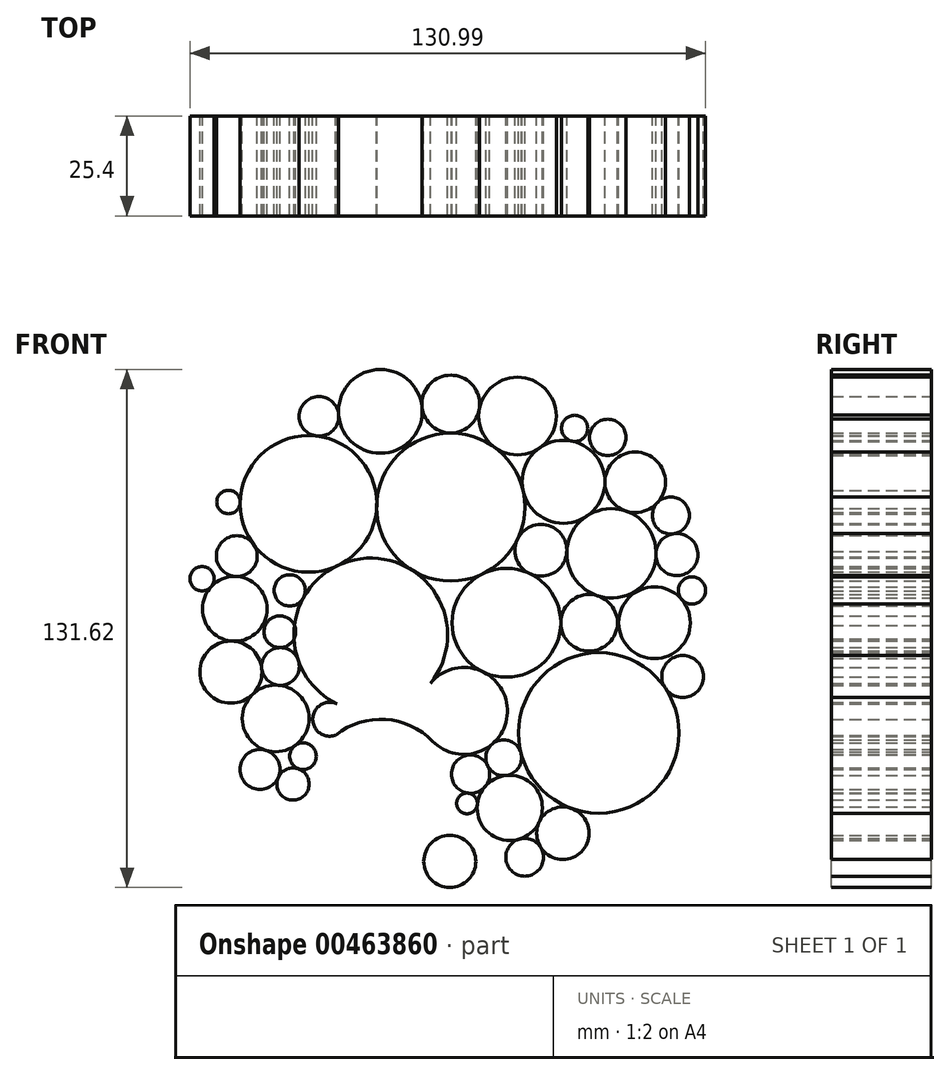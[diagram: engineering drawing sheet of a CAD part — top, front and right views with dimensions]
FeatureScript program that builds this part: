
annotation { "Feature Type Name" : "Feature", "Feature Type Description" : "" }
export const myFeature = defineFeature(function(context is Context, id is Id, definition is map)
    precondition{}
    {
        {
            var Q0;
            Q0=qCreatedBy(makeId("Front.planeOp"),FACE);
            var sketch = newSketch(context, id + "F0", { "sketchPlane" : qUnion([Q0])});
            skCircle(sketch, "E0", {"center": v(0, 0) * mm, "radius": 67.26 * mm});
            skCircle(sketch, "E1", {"center": v(-17.9, 53.72) * mm, "radius": 10.64 * mm});
            skCircle(sketch, "E2", {"center": v(-36.15, 30.22) * mm, "radius": 17.35 * mm});
            skCircle(sketch, "E3", {"center": v(46.85, 35.7) * mm, "radius": 7.69 * mm});
            skCircle(sketch, "E4", {"center": v(40.82, 17.65) * mm, "radius": 11.35 * mm});
            skCircle(sketch, "E5", {"center": v(0, 29.4) * mm, "radius": 18.81 * mm});
            skCircle(sketch, "E6", {"center": v(37.58, -28) * mm, "radius": 20.4 * mm});
            skCircle(sketch, "E7", {"center": v(-63.2, 11.2) * mm, "radius": 3.08 * mm});
            skArc(sketch, "E8", {"start": v(54.82, -38.89) * mm, "mid": v(54.84, -38.9) * mm, "end": v(54.86, -38.91) * mm});
            skCircle(sketch, "E9", {"center": v(-20.34, -3.08) * mm, "radius": 19.52 * mm});
            skCircle(sketch, "E10", {"center": v(14.13, 0) * mm, "radius": 13.81 * mm});
            skCircle(sketch, "E11", {"center": v(16.95, 52.54) * mm, "radius": 9.87 * mm});
            skCircle(sketch, "E12", {"center": v(-55.87, -12.54) * mm, "radius": 7.89 * mm});
            skCircle(sketch, "E13", {"center": v(51.75, 0) * mm, "radius": 9.1 * mm});
            skCircle(sketch, "E14", {"center": v(28.63, 35.82) * mm, "radius": 10.53 * mm});
            skCircle(sketch, "E15", {"center": v(28.48, -53.48) * mm, "radius": 6.67 * mm});
            skCircle(sketch, "E16", {"center": v(3.34, -22.4) * mm, "radius": 11.05 * mm});
            skCircle(sketch, "E17", {"center": v(13.44, -34.29) * mm, "radius": 4.55 * mm});
            skCircle(sketch, "E18", {"center": v(-44.5, -24.3) * mm, "radius": 8.48 * mm});
            skCircle(sketch, "E19", {"center": v(-54.9, 3.54) * mm, "radius": 8.21 * mm});
            skCircle(sketch, "E20", {"center": v(-33.5, 52.44) * mm, "radius": 5.03 * mm});
            skCircle(sketch, "E21", {"center": v(35.14, 0) * mm, "radius": 7.2 * mm});
            skCircle(sketch, "E22", {"center": v(-0.25, -60.64) * mm, "radius": 6.62 * mm});
            skCircle(sketch, "E23", {"center": v(57.44, 17.33) * mm, "radius": 5.35 * mm});
            skCircle(sketch, "E24", {"center": v(58.9, -13.65) * mm, "radius": 5.3 * mm});
            skCircle(sketch, "E25", {"center": v(22.9, 18.42) * mm, "radius": 6.59 * mm});
            skCircle(sketch, "E26", {"center": v(-54.36, 16.93) * mm, "radius": 5.2 * mm});
            skCircle(sketch, "E27", {"center": v(-56.48, 30.68) * mm, "radius": 2.98 * mm});
            skCircle(sketch, "E28", {"center": v(-43.42, -2.28) * mm, "radius": 4.03 * mm});
            skCircle(sketch, "E29", {"center": v(-43.28, -11.1) * mm, "radius": 4.79 * mm});
            skCircle(sketch, "E30", {"center": v(-48.49, -37.27) * mm, "radius": 5.08 * mm});
            skCircle(sketch, "E31", {"center": v(31.47, 49.4) * mm, "radius": 3.33 * mm});
            skCircle(sketch, "E32", {"center": v(0, 55.57) * mm, "radius": 7.35 * mm});
            skCircle(sketch, "E33", {"center": v(14.98, -47.04) * mm, "radius": 8.3 * mm});
            skCircle(sketch, "E34", {"center": v(-30.76, -24.52) * mm, "radius": 4.32 * mm});
            skCircle(sketch, "E35", {"center": v(-40.1, -40.97) * mm, "radius": 4.09 * mm});
            skCircle(sketch, "E36", {"center": v(18.77, -59.57) * mm, "radius": 4.8 * mm});
            skCircle(sketch, "E37", {"center": v(55.9, 27.26) * mm, "radius": 4.7 * mm});
            skCircle(sketch, "E38", {"center": v(61.26, 8.22) * mm, "radius": 3.46 * mm});
            skCircle(sketch, "E39", {"center": v(-17.75, -42.85) * mm, "radius": 18.33 * mm});
            skCircle(sketch, "E40", {"center": v(-40.92, 8.24) * mm, "radius": 3.97 * mm});
            skCircle(sketch, "E41", {"center": v(5.02, -38.46) * mm, "radius": 4.85 * mm});
            skCircle(sketch, "E42", {"center": v(4.1, -45.9) * mm, "radius": 2.64 * mm});
            skCircle(sketch, "E43", {"center": v(39.89, 47.1) * mm, "radius": 4.62 * mm});
            skCircle(sketch, "E44", {"center": v(-37.54, -33.9) * mm, "radius": 3.38 * mm});
            skSolve(sketch);
        }
        {
            var Q0;
            {var subQ0=sQuery(id+"F0.wireOp",EDGE,"E5");var subQ6=makeQuery(id+"F0.imprint","INTERSECT",VERTEX,{"derivedFrom":[subQ0,sQuery(id+"F0.wireOp",EDGE,"E11")]});Q0=makeQuery(id+"F0.imprint","IMPRINT",FACE,{"disambiguationData":[TD([[makeQuery(id+"F0.imprint","IMPRINT",EDGE,{"disambiguationData":[TD([[subQ6,1.0]])],"derivedFrom":subQ0}),1.0]])]});}
            var sketch = newSketch(context, id + "F1", { "sketchPlane" : qUnion([Q0])});
            skSolve(sketch);
        }
        {
            var Q0;
            Q0 = qSketchRegion(id + "F1", true);
            var Q1;
            {var subQ0=sQuery(id+"F0.wireOp",EDGE,"E5");var subQ4=makeQuery(id+"F0.imprint","INTERSECT",VERTEX,{"derivedFrom":[subQ0,sQuery(id+"F0.wireOp",EDGE,"E11")]});Q1=makeQuery(id+"F1.imprint","IMPRINT",FACE,{"disambiguationData":[TD([[makeQuery(id+"F1.imprint","IMPRINT",EDGE,{"derivedFrom":makeQuery(id+"F0.imprint","IMPRINT",EDGE,{"disambiguationData":[TD([[subQ4,1.0]])],"derivedFrom":subQ0})}),1.0]])]});}
            var Q2;
            {var subQ0=sQuery(id+"F0.wireOp",EDGE,"E2");var subQ4=makeQuery(id+"F0.imprint","INTERSECT",VERTEX,{"derivedFrom":[subQ0,sQuery(id+"F0.wireOp",EDGE,"E27")]});Q2=makeQuery(id+"F0.imprint","IMPRINT",FACE,{"disambiguationData":[TD([[makeQuery(id+"F0.imprint","IMPRINT",EDGE,{"disambiguationData":[TD([[subQ4,1.0]])],"derivedFrom":subQ0}),1.0]])]});}
            var Q3;
            {var subQ0=sQuery(id+"F0.wireOp",EDGE,"E1");var subQ1=makeQuery(id+"F0.imprint","INTERSECT",VERTEX,{"derivedFrom":[sQuery(id+"F0.wireOp",EDGE,"E0"),subQ0]});Q3=makeQuery(id+"F0.imprint","IMPRINT",FACE,{"disambiguationData":[TD([[makeQuery(id+"F0.imprint","IMPRINT",EDGE,{"disambiguationData":[TD([[subQ1,1.0]])],"derivedFrom":subQ0}),1.0]])]});}
            var Q4;
            {var subQ0=sQuery(id+"F0.wireOp",EDGE,"E32");var subQ1=makeQuery(id+"F0.imprint","INTERSECT",VERTEX,{"derivedFrom":[sQuery(id+"F0.wireOp",EDGE,"E1"),subQ0]});Q4=makeQuery(id+"F0.imprint","IMPRINT",FACE,{"disambiguationData":[TD([[makeQuery(id+"F0.imprint","IMPRINT",EDGE,{"disambiguationData":[TD([[subQ1,-1.0]])],"derivedFrom":subQ0}),1.0]])]});}
            var Q5;
            {var subQ0=sQuery(id+"F0.wireOp",EDGE,"E15");var subQ1=makeQuery(id+"F0.imprint","INTERSECT",VERTEX,{"derivedFrom":[sQuery(id+"F0.wireOp",EDGE,"E6"),subQ0]});Q5=makeQuery(id+"F0.imprint","IMPRINT",FACE,{"disambiguationData":[TD([[makeQuery(id+"F0.imprint","IMPRINT",EDGE,{"disambiguationData":[TD([[subQ1,-1.0]])],"derivedFrom":subQ0}),1.0]])]});}
            var Q6;
            {var subQ0=sQuery(id+"F0.wireOp",EDGE,"E6");var subQ5=makeQuery(id+"F0.imprint","INTERSECT",VERTEX,{"derivedFrom":[subQ0,sQuery(id+"F0.wireOp",EDGE,"E24")]});Q6=makeQuery(id+"F0.imprint","IMPRINT",FACE,{"disambiguationData":[TD([[makeQuery(id+"F0.imprint","IMPRINT",EDGE,{"disambiguationData":[TD([[subQ5,-1.0]])],"derivedFrom":subQ0}),1.0]])]});}
            var Q7;
            {var subQ0=sQuery(id+"F0.wireOp",EDGE,"E21");var subQ1=makeQuery(id+"F0.imprint","INTERSECT",VERTEX,{"derivedFrom":[sQuery(id+"F0.wireOp",EDGE,"E4"),subQ0]});Q7=makeQuery(id+"F0.imprint","IMPRINT",FACE,{"disambiguationData":[TD([[makeQuery(id+"F0.imprint","IMPRINT",EDGE,{"disambiguationData":[TD([[subQ1,-1.0]])],"derivedFrom":subQ0}),1.0]])]});}
            var Q8;
            {var subQ0=sQuery(id+"F0.wireOp",EDGE,"E4");var subQ4=makeQuery(id+"F0.imprint","INTERSECT",VERTEX,{"derivedFrom":[sQuery(id+"F0.wireOp",EDGE,"E3"),subQ0]});Q8=makeQuery(id+"F0.imprint","IMPRINT",FACE,{"disambiguationData":[TD([[makeQuery(id+"F0.imprint","IMPRINT",EDGE,{"disambiguationData":[TD([[subQ4,1.0]])],"derivedFrom":subQ0}),1.0]])]});}
            var Q9;
            Q9=makeQuery(id+"F0.imprint","IMPRINT",FACE,{"disambiguationData":[TD([[makeQuery(id+"F0.imprint","IMPRINT",EDGE,{"derivedFrom":sQuery(id+"F0.wireOp",EDGE,"E13")}),1.0]])]});
            var Q10;
            Q10=makeQuery(id+"F0.imprint","IMPRINT",FACE,{"disambiguationData":[TD([[makeQuery(id+"F0.imprint","IMPRINT",EDGE,{"derivedFrom":sQuery(id+"F0.wireOp",EDGE,"E38")}),1.0]])]});
            var Q11;
            {var subQ0=sQuery(id+"F0.wireOp",EDGE,"E23");var subQ1=sQuery(id+"F0.wireOp",EDGE,"E4");var subQ2=makeQuery(id+"F0.imprint","INTERSECT",VERTEX,{"disambiguationData":[OD(0.0)],"derivedFrom":[subQ1,subQ0]});Q11=makeQuery(id+"F0.imprint","IMPRINT",FACE,{"disambiguationData":[TD([[makeQuery(id+"F0.imprint","IMPRINT",EDGE,{"disambiguationData":[TD([[subQ2,1.0]])],"derivedFrom":subQ1}),-1.0]])]});}
            var Q12;
            {var subQ0=sQuery(id+"F0.wireOp",EDGE,"E37");var subQ1=makeQuery(id+"F0.imprint","INTERSECT",VERTEX,{"derivedFrom":[sQuery(id+"F0.wireOp",EDGE,"E3"),subQ0]});Q12=makeQuery(id+"F0.imprint","IMPRINT",FACE,{"disambiguationData":[TD([[makeQuery(id+"F0.imprint","IMPRINT",EDGE,{"disambiguationData":[TD([[subQ1,-1.0]])],"derivedFrom":subQ0}),1.0]])]});}
            var Q13;
            {var subQ0=sQuery(id+"F0.wireOp",EDGE,"E3");var subQ1=makeQuery(id+"F0.imprint","INTERSECT",VERTEX,{"derivedFrom":[subQ0,sQuery(id+"F0.wireOp",EDGE,"E4")]});Q13=makeQuery(id+"F0.imprint","IMPRINT",FACE,{"disambiguationData":[TD([[makeQuery(id+"F0.imprint","IMPRINT",EDGE,{"disambiguationData":[TD([[subQ1,1.0]])],"derivedFrom":subQ0}),1.0]])]});}
            var Q14;
            Q14=makeQuery(id+"F0.imprint","IMPRINT",FACE,{"disambiguationData":[TD([[makeQuery(id+"F0.imprint","IMPRINT",EDGE,{"derivedFrom":sQuery(id+"F0.wireOp",EDGE,"E43")}),1.0]])]});
            var Q15;
            {var subQ0=sQuery(id+"F0.wireOp",EDGE,"E14");var subQ5=makeQuery(id+"F0.imprint","INTERSECT",VERTEX,{"derivedFrom":[subQ0,sQuery(id+"F0.wireOp",EDGE,"E31")]});Q15=makeQuery(id+"F0.imprint","IMPRINT",FACE,{"disambiguationData":[TD([[makeQuery(id+"F0.imprint","IMPRINT",EDGE,{"disambiguationData":[TD([[subQ5,-1.0]])],"derivedFrom":subQ0}),1.0]])]});}
            var Q16;
            {var subQ0=sQuery(id+"F0.wireOp",EDGE,"E11");var subQ1=makeQuery(id+"F0.imprint","INTERSECT",VERTEX,{"derivedFrom":[sQuery(id+"F0.wireOp",EDGE,"E5"),subQ0]});Q16=makeQuery(id+"F0.imprint","IMPRINT",FACE,{"disambiguationData":[TD([[makeQuery(id+"F0.imprint","IMPRINT",EDGE,{"disambiguationData":[TD([[subQ1,1.0]])],"derivedFrom":subQ0}),1.0]])]});}
            var Q17;
            Q17=makeQuery(id+"F0.imprint","IMPRINT",FACE,{"disambiguationData":[TD([[makeQuery(id+"F0.imprint","IMPRINT",EDGE,{"derivedFrom":sQuery(id+"F0.wireOp",EDGE,"E24")}),1.0]])]});
            var Q18;
            {var subQ0=sQuery(id+"F0.wireOp",EDGE,"E25");var subQ1=makeQuery(id+"F0.imprint","INTERSECT",VERTEX,{"derivedFrom":[sQuery(id+"F0.wireOp",EDGE,"E5"),subQ0]});Q18=makeQuery(id+"F0.imprint","IMPRINT",FACE,{"disambiguationData":[TD([[makeQuery(id+"F0.imprint","IMPRINT",EDGE,{"disambiguationData":[TD([[subQ1,-1.0]])],"derivedFrom":subQ0}),1.0]])]});}
            var Q19;
            {var subQ0=sQuery(id+"F0.wireOp",EDGE,"E10");var subQ1=makeQuery(id+"F0.imprint","INTERSECT",VERTEX,{"derivedFrom":[subQ0,sQuery(id+"F0.wireOp",EDGE,"E25")]});Q19=makeQuery(id+"F0.imprint","IMPRINT",FACE,{"disambiguationData":[TD([[makeQuery(id+"F0.imprint","IMPRINT",EDGE,{"disambiguationData":[TD([[subQ1,1.0]])],"derivedFrom":subQ0}),1.0]])]});}
            var Q20;
            {var subQ0=sQuery(id+"F0.wireOp",EDGE,"E16");var subQ1=makeQuery(id+"F0.imprint","INTERSECT",VERTEX,{"derivedFrom":[sQuery(id+"F0.wireOp",EDGE,"E9"),subQ0]});Q20=makeQuery(id+"F0.imprint","IMPRINT",FACE,{"disambiguationData":[TD([[makeQuery(id+"F0.imprint","IMPRINT",EDGE,{"disambiguationData":[TD([[subQ1,1.0]])],"derivedFrom":subQ0}),1.0]])]});}
            var Q21;
            {var subQ0=sQuery(id+"F0.wireOp",EDGE,"E34");var subQ1=makeQuery(id+"F0.imprint","INTERSECT",VERTEX,{"derivedFrom":[sQuery(id+"F0.wireOp",EDGE,"E9"),subQ0]});Q21=makeQuery(id+"F0.imprint","IMPRINT",FACE,{"disambiguationData":[TD([[makeQuery(id+"F0.imprint","IMPRINT",EDGE,{"disambiguationData":[TD([[subQ1,-1.0]])],"derivedFrom":subQ0}),1.0]])]});}
            var Q22;
            {var subQ0=sQuery(id+"F0.wireOp",EDGE,"E18");var subQ1=makeQuery(id+"F0.imprint","INTERSECT",VERTEX,{"derivedFrom":[sQuery(id+"F0.wireOp",EDGE,"E12"),subQ0]});Q22=makeQuery(id+"F0.imprint","IMPRINT",FACE,{"disambiguationData":[TD([[makeQuery(id+"F0.imprint","IMPRINT",EDGE,{"disambiguationData":[TD([[subQ1,1.0]])],"derivedFrom":subQ0}),1.0]])]});}
            var Q23;
            {var subQ0=sQuery(id+"F0.wireOp",EDGE,"E30");var subQ1=makeQuery(id+"F0.imprint","INTERSECT",VERTEX,{"derivedFrom":[sQuery(id+"F0.wireOp",EDGE,"E18"),subQ0]});Q23=makeQuery(id+"F0.imprint","IMPRINT",FACE,{"disambiguationData":[TD([[makeQuery(id+"F0.imprint","IMPRINT",EDGE,{"disambiguationData":[TD([[subQ1,-1.0]])],"derivedFrom":subQ0}),1.0]])]});}
            var Q24;
            {var subQ0=sQuery(id+"F0.wireOp",EDGE,"E44");var subQ1=makeQuery(id+"F0.imprint","INTERSECT",VERTEX,{"derivedFrom":[sQuery(id+"F0.wireOp",EDGE,"E18"),subQ0]});Q24=makeQuery(id+"F0.imprint","IMPRINT",FACE,{"disambiguationData":[TD([[makeQuery(id+"F0.imprint","IMPRINT",EDGE,{"disambiguationData":[TD([[subQ1,-1.0]])],"derivedFrom":subQ0}),1.0]])]});}
            var Q25;
            {var subQ0=sQuery(id+"F0.wireOp",EDGE,"E35");var subQ1=makeQuery(id+"F0.imprint","INTERSECT",VERTEX,{"derivedFrom":[sQuery(id+"F0.wireOp",EDGE,"E30"),subQ0]});Q25=makeQuery(id+"F0.imprint","IMPRINT",FACE,{"disambiguationData":[TD([[makeQuery(id+"F0.imprint","IMPRINT",EDGE,{"disambiguationData":[TD([[subQ1,-1.0]])],"derivedFrom":subQ0}),1.0]])]});}
            var Q26;
            {var subQ0=sQuery(id+"F0.wireOp",EDGE,"E22");var subQ1=makeQuery(id+"F0.imprint","INTERSECT",VERTEX,{"derivedFrom":[sQuery(id+"F0.wireOp",EDGE,"E0"),subQ0]});Q26=makeQuery(id+"F0.imprint","IMPRINT",FACE,{"disambiguationData":[TD([[makeQuery(id+"F0.imprint","IMPRINT",EDGE,{"disambiguationData":[TD([[subQ1,1.0]])],"derivedFrom":subQ0}),1.0]])]});}
            var Q27;
            {var subQ0=sQuery(id+"F0.wireOp",EDGE,"E42");var subQ1=makeQuery(id+"F0.imprint","INTERSECT",VERTEX,{"derivedFrom":[sQuery(id+"F0.wireOp",EDGE,"E33"),subQ0]});Q27=makeQuery(id+"F0.imprint","IMPRINT",FACE,{"disambiguationData":[TD([[makeQuery(id+"F0.imprint","IMPRINT",EDGE,{"disambiguationData":[TD([[subQ1,1.0]])],"derivedFrom":subQ0}),1.0]])]});}
            var Q28;
            {var subQ0=sQuery(id+"F0.wireOp",EDGE,"E41");var subQ1=makeQuery(id+"F0.imprint","INTERSECT",VERTEX,{"derivedFrom":[sQuery(id+"F0.wireOp",EDGE,"E17"),subQ0]});Q28=makeQuery(id+"F0.imprint","IMPRINT",FACE,{"disambiguationData":[TD([[makeQuery(id+"F0.imprint","IMPRINT",EDGE,{"disambiguationData":[TD([[subQ1,-1.0]])],"derivedFrom":subQ0}),1.0]])]});}
            var Q29;
            {var subQ0=sQuery(id+"F0.wireOp",EDGE,"E17");var subQ1=makeQuery(id+"F0.imprint","INTERSECT",VERTEX,{"derivedFrom":[sQuery(id+"F0.wireOp",EDGE,"E6"),subQ0]});Q29=makeQuery(id+"F0.imprint","IMPRINT",FACE,{"disambiguationData":[TD([[makeQuery(id+"F0.imprint","IMPRINT",EDGE,{"disambiguationData":[TD([[subQ1,-1.0]])],"derivedFrom":subQ0}),1.0]])]});}
            var Q30;
            {var subQ0=sQuery(id+"F0.wireOp",EDGE,"E33");var subQ5=makeQuery(id+"F0.imprint","INTERSECT",VERTEX,{"derivedFrom":[sQuery(id+"F0.wireOp",EDGE,"E17"),subQ0]});Q30=makeQuery(id+"F0.imprint","IMPRINT",FACE,{"disambiguationData":[TD([[makeQuery(id+"F0.imprint","IMPRINT",EDGE,{"disambiguationData":[TD([[subQ5,-1.0]])],"derivedFrom":subQ0}),1.0]])]});}
            var Q31;
            {var subQ0=sQuery(id+"F0.wireOp",EDGE,"E36");var subQ1=makeQuery(id+"F0.imprint","INTERSECT",VERTEX,{"derivedFrom":[sQuery(id+"F0.wireOp",EDGE,"E15"),subQ0]});Q31=makeQuery(id+"F0.imprint","IMPRINT",FACE,{"disambiguationData":[TD([[makeQuery(id+"F0.imprint","IMPRINT",EDGE,{"disambiguationData":[TD([[subQ1,-1.0]])],"derivedFrom":subQ0}),1.0]])]});}
            var Q32;
            {var subQ1=sQuery(id+"F0.wireOp",EDGE,"E9");var subQ6=makeQuery(id+"F0.imprint","INTERSECT",VERTEX,{"derivedFrom":[sQuery(id+"F0.wireOp",EDGE,"E2"),subQ1]});Q32=makeQuery(id+"F0.imprint","IMPRINT",FACE,{"disambiguationData":[TD([[makeQuery(id+"F0.imprint","IMPRINT",EDGE,{"disambiguationData":[TD([[subQ6,1.0]])],"derivedFrom":subQ1}),1.0]])]});}
            var Q33;
            {var subQ0=sQuery(id+"F0.wireOp",EDGE,"E26");var subQ1=makeQuery(id+"F0.imprint","INTERSECT",VERTEX,{"derivedFrom":[sQuery(id+"F0.wireOp",EDGE,"E2"),subQ0]});Q33=makeQuery(id+"F0.imprint","IMPRINT",FACE,{"disambiguationData":[TD([[makeQuery(id+"F0.imprint","IMPRINT",EDGE,{"disambiguationData":[TD([[subQ1,-1.0]])],"derivedFrom":subQ0}),1.0]])]});}
            var Q34;
            {var subQ0=sQuery(id+"F0.wireOp",EDGE,"E7");var subQ1=makeQuery(id+"F0.imprint","INTERSECT",VERTEX,{"derivedFrom":[sQuery(id+"F0.wireOp",EDGE,"E0"),subQ0]});Q34=makeQuery(id+"F0.imprint","IMPRINT",FACE,{"disambiguationData":[TD([[makeQuery(id+"F0.imprint","IMPRINT",EDGE,{"disambiguationData":[TD([[subQ1,-1.0]])],"derivedFrom":subQ0}),1.0]])]});}
            var Q35;
            {var subQ0=sQuery(id+"F0.wireOp",EDGE,"E19");var subQ1=makeQuery(id+"F0.imprint","INTERSECT",VERTEX,{"derivedFrom":[sQuery(id+"F0.wireOp",EDGE,"E7"),subQ0]});Q35=makeQuery(id+"F0.imprint","IMPRINT",FACE,{"disambiguationData":[TD([[makeQuery(id+"F0.imprint","IMPRINT",EDGE,{"disambiguationData":[TD([[subQ1,1.0]])],"derivedFrom":subQ0}),1.0]])]});}
            var Q36;
            {var subQ0=sQuery(id+"F0.wireOp",EDGE,"E27");var subQ1=makeQuery(id+"F0.imprint","INTERSECT",VERTEX,{"derivedFrom":[sQuery(id+"F0.wireOp",EDGE,"E0"),subQ0]});Q36=makeQuery(id+"F0.imprint","IMPRINT",FACE,{"disambiguationData":[TD([[makeQuery(id+"F0.imprint","IMPRINT",EDGE,{"disambiguationData":[TD([[subQ1,-1.0]])],"derivedFrom":subQ0}),1.0]])]});}
            var Q37;
            Q37=makeQuery(id+"F0.imprint","IMPRINT",FACE,{"disambiguationData":[TD([[makeQuery(id+"F0.imprint","IMPRINT",EDGE,{"derivedFrom":sQuery(id+"F0.wireOp",EDGE,"E40")}),1.0]])]});
            var Q38;
            {var subQ0=sQuery(id+"F0.wireOp",EDGE,"E28");var subQ1=sQuery(id+"F0.wireOp",EDGE,"E9");var subQ2=makeQuery(id+"F0.imprint","INTERSECT",VERTEX,{"disambiguationData":[OD(0.0)],"derivedFrom":[subQ1,subQ0]});Q38=makeQuery(id+"F0.imprint","IMPRINT",FACE,{"disambiguationData":[TD([[makeQuery(id+"F0.imprint","IMPRINT",EDGE,{"disambiguationData":[TD([[subQ2,-1.0]])],"derivedFrom":subQ1}),-1.0]])]});}
            var Q39;
            {var subQ0=sQuery(id+"F0.wireOp",EDGE,"E29");var subQ1=makeQuery(id+"F0.imprint","INTERSECT",VERTEX,{"derivedFrom":[sQuery(id+"F0.wireOp",EDGE,"E9"),subQ0]});Q39=makeQuery(id+"F0.imprint","IMPRINT",FACE,{"disambiguationData":[TD([[makeQuery(id+"F0.imprint","IMPRINT",EDGE,{"disambiguationData":[TD([[subQ1,-1.0]])],"derivedFrom":subQ0}),1.0]])]});}
            var Q40;
            {var subQ0=sQuery(id+"F0.wireOp",EDGE,"E12");var subQ1=makeQuery(id+"F0.imprint","INTERSECT",VERTEX,{"derivedFrom":[subQ0,sQuery(id+"F0.wireOp",EDGE,"E19")]});Q40=makeQuery(id+"F0.imprint","IMPRINT",FACE,{"disambiguationData":[TD([[makeQuery(id+"F0.imprint","IMPRINT",EDGE,{"disambiguationData":[TD([[subQ1,1.0]])],"derivedFrom":subQ0}),1.0]])]});}
            var Q41;
            {var subQ0=sQuery(id+"F0.wireOp",EDGE,"E39");var subQ1=sQuery(id+"F0.wireOp",EDGE,"E34");var subQ2=makeQuery(id+"F0.imprint","INTERSECT",VERTEX,{"disambiguationData":[OD(0.0)],"derivedFrom":[subQ1,subQ0]});Q41=makeQuery(id+"F0.imprint","IMPRINT",FACE,{"disambiguationData":[TD([[makeQuery(id+"F0.imprint","IMPRINT",EDGE,{"disambiguationData":[TD([[subQ2,-1.0]])],"derivedFrom":subQ1}),-1.0]])]});}
            var Q42;
            {var subQ0=sQuery(id+"F0.wireOp",EDGE,"E20");var subQ1=makeQuery(id+"F0.imprint","INTERSECT",VERTEX,{"derivedFrom":[sQuery(id+"F0.wireOp",EDGE,"E0"),subQ0]});Q42=makeQuery(id+"F0.imprint","IMPRINT",FACE,{"disambiguationData":[TD([[makeQuery(id+"F0.imprint","IMPRINT",EDGE,{"disambiguationData":[TD([[subQ1,1.0]])],"derivedFrom":subQ0}),1.0]])]});}
            var Q43;
            Q43=makeQuery(id+"F0.imprint","IMPRINT",FACE,{"disambiguationData":[TD([[makeQuery(id+"F0.imprint","IMPRINT",EDGE,{"derivedFrom":sQuery(id+"F0.wireOp",EDGE,"E31")}),1.0]])]});
            extrude(context, id + "F2", {"entities" : qUnion([Q0, Q1, Q2, Q3, Q4, Q5, Q6, Q7, Q8, Q9, Q10, Q11, Q12, Q13, Q14, Q15, Q16, Q17, Q18, Q19, Q20, Q21, Q22, Q23, Q24, Q25, Q26, Q27, Q28, Q29, Q30, Q31, Q32, Q33, Q34, Q35, Q36, Q37, Q38, Q39, Q40, Q41, Q42, Q43]), "depth" : 25.4 * mm});
        }
    });
